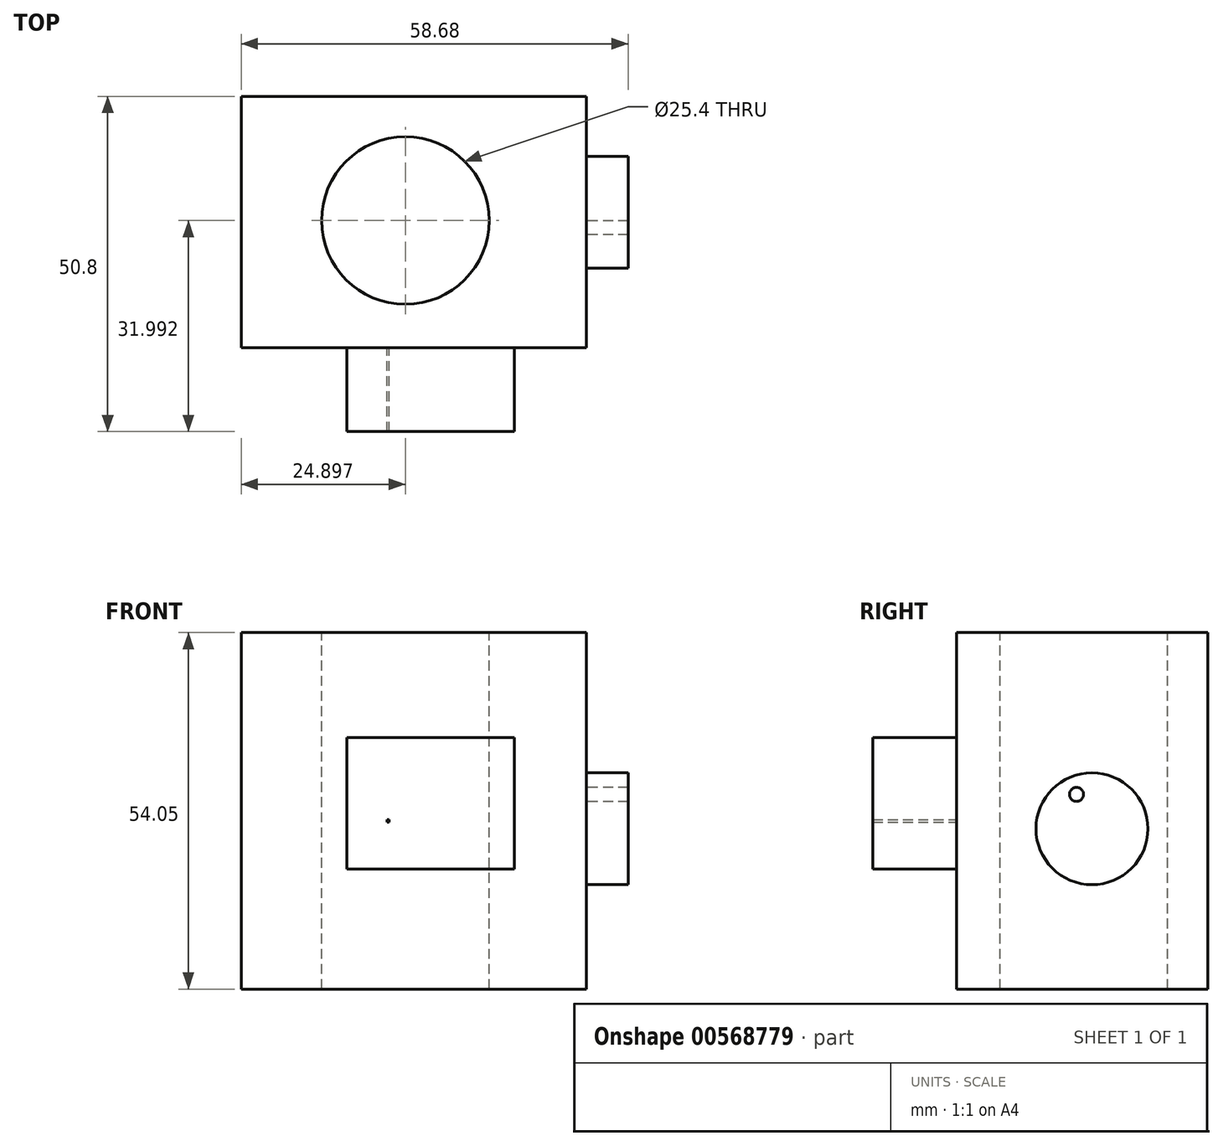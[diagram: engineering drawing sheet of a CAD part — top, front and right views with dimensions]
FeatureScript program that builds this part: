
annotation { "Feature Type Name" : "Feature", "Feature Type Description" : "" }
export const myFeature = defineFeature(function(context is Context, id is Id, definition is map)
    precondition{}
    {
        {
            var Q0;
            Q0=qCreatedBy(makeId("Front.planeOp"),FACE);
            var sketch = newSketch(context, id + "F0", { "sketchPlane" : qUnion([Q0])});
            skLineSegment(sketch, "E0.bottom", {"start": v(0, 0) * mm, "end": v(-52.33, 0) * mm});
            skLineSegment(sketch, "E0.top", {"start": v(0, 54.05) * mm, "end": v(-52.33, 54.05) * mm});
            skLineSegment(sketch, "E0.left", {"start": v(0, 0) * mm, "end": v(0, 54.05) * mm});
            skLineSegment(sketch, "E0.right", {"start": v(-52.33, 0) * mm, "end": v(-52.33, 54.05) * mm});
            skSolve(sketch);
        }
        {
            var Q0;
            Q0 = qSketchRegion(id + "F0", true);
            extrude(context, id + "F1", {"entities" : qUnion([Q0]), "depth" : 38.1 * mm, "offsetDistance" : 25.4 * mm});
        }
        {
            var Q0;
            Q0=makeQuery(id+"F1.opExtrude","SWEPT_FACE",FACE,{"disambiguationData":[OSD([sQuery(id+"F0.wireOp",EDGE,"E0.top")])]});
            var sketch = newSketch(context, id + "F2", { "sketchPlane" : qUnion([Q0])});
            skCircle(sketch, "E1", {"center": v(-27.43, -18.8) * mm, "radius": 10.38 * mm});
            skSolve(sketch);
        }
        {
            var Q0;
            Q0=sQuery(id+"F2.wireOp",VERTEX,"E1.center");
            var Q1;
            Q1=makeQuery(id+"F1.opExtrude","SWEPT_BODY",BODY,{"disambiguationData":[OSD([sQuery(id+"F0.wireOp",EDGE,"E0.bottom"),sQuery(id+"F0.wireOp",EDGE,"E0.top"),sQuery(id+"F0.wireOp",EDGE,"E0.left"),sQuery(id+"F0.wireOp",EDGE,"E0.right")])]});
            hole(context, id + "F3", {"style" : HoleStyle.SIMPLE, "endStyle" : HoleEndStyle.THROUGH, "holeDiameter" : 25.4 * mm, "isTappedThrough" : true, "tappedDepth" : 12.7 * mm, "tapClearance" : 3, "locations" : qUnion([Q0]), "scope" : qUnion([Q1])});
        }
        {
            var Q0;
            Q0=makeQuery(id+"F1.opExtrude","CAP_FACE",FACE,{"disambiguationData":[OSD([sQuery(id+"F0.wireOp",EDGE,"E0.bottom"),sQuery(id+"F0.wireOp",EDGE,"E0.top"),sQuery(id+"F0.wireOp",EDGE,"E0.left"),sQuery(id+"F0.wireOp",EDGE,"E0.right")])],"isStart":false});
            var sketch = newSketch(context, id + "F4", { "sketchPlane" : qUnion([Q0])});
            skLineSegment(sketch, "E2.bottom", {"start": v(-10.92, 18.23) * mm, "end": v(-36.32, 18.23) * mm});
            skLineSegment(sketch, "E2.top", {"start": v(-10.92, 38.17) * mm, "end": v(-36.32, 38.17) * mm});
            skLineSegment(sketch, "E2.left", {"start": v(-10.92, 18.23) * mm, "end": v(-10.92, 38.17) * mm});
            skLineSegment(sketch, "E2.right", {"start": v(-36.32, 18.23) * mm, "end": v(-36.32, 38.17) * mm});
            skLineSegment(sketch, "E3.bottom", {"start": v(-29.87, 25.7) * mm, "end": v(-30.23, 25.7) * mm});
            skLineSegment(sketch, "E3.top", {"start": v(-29.87, 25.34) * mm, "end": v(-30.23, 25.34) * mm});
            skLineSegment(sketch, "E3.left", {"start": v(-29.87, 25.7) * mm, "end": v(-29.87, 25.34) * mm});
            skLineSegment(sketch, "E3.right", {"start": v(-30.23, 25.7) * mm, "end": v(-30.23, 25.34) * mm});
            skSolve(sketch);
        }
        {
            var Q0;
            Q0=makeQuery(id+"F4.imprint","IMPRINT",FACE,{"disambiguationData":[TD([[makeQuery(id+"F4.imprint","IMPRINT",EDGE,{"derivedFrom":sQuery(id+"F4.wireOp",EDGE,"E2.bottom")}),-1.0]])]});
            extrude(context, id + "F5", {"entities" : qUnion([Q0]), "operationType" : NewBodyOperationType.ADD, "depth" : 12.7 * mm, "offsetDistance" : 25.4 * mm});
        }
        {
            var Q0;
            Q0=makeQuery(id+"F1.opExtrude","SWEPT_FACE",FACE,{"disambiguationData":[OSD([sQuery(id+"F0.wireOp",EDGE,"E0.left")])]});
            var sketch = newSketch(context, id + "F6", { "sketchPlane" : qUnion([Q0])});
            skCircle(sketch, "E4", {"center": v(-17.56, 24.31) * mm, "radius": 8.49 * mm});
            skCircle(sketch, "E5", {"center": v(-19.9, 29.52) * mm, "radius": 1.07 * mm});
            skSolve(sketch);
        }
        {
            var Q0;
            Q0=makeQuery(id+"F6.imprint","IMPRINT",FACE,{"disambiguationData":[TD([[makeQuery(id+"F6.imprint","IMPRINT",EDGE,{"derivedFrom":sQuery(id+"F6.wireOp",EDGE,"E4")}),1.0]])]});
            extrude(context, id + "F7", {"entities" : qUnion([Q0]), "operationType" : NewBodyOperationType.ADD, "depth" : 6.35 * mm, "offsetDistance" : 25.4 * mm});
        }
    });
